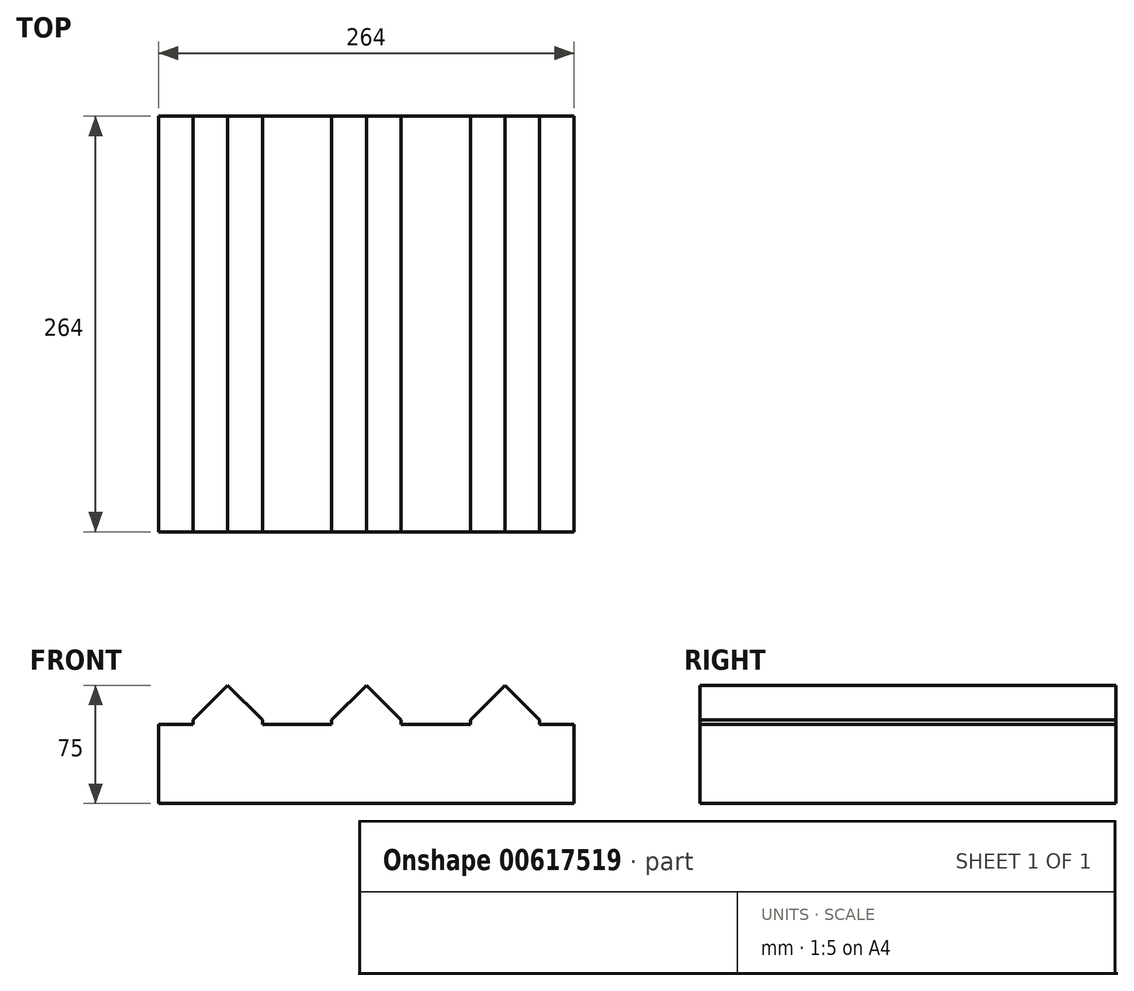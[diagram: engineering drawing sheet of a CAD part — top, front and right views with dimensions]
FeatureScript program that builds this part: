
annotation { "Feature Type Name" : "Feature", "Feature Type Description" : "" }
export const myFeature = defineFeature(function(context is Context, id is Id, definition is map)
    precondition{}
    {
        {
            var Q0;
            Q0=qCreatedBy(makeId("Top.planeOp"),FACE);
            var sketch = newSketch(context, id + "F0", { "sketchPlane" : qUnion([Q0])});
            skLineSegment(sketch, "E0.bottom", {"start": v(22, -22) * mm, "end": v(-22, -22) * mm});
            skLineSegment(sketch, "E0.top", {"start": v(22, 22) * mm, "end": v(-22, 22) * mm});
            skLineSegment(sketch, "E0.left", {"start": v(22, -22) * mm, "end": v(22, 22) * mm});
            skLineSegment(sketch, "E0.right", {"start": v(-22, -22) * mm, "end": v(-22, 22) * mm});
            skPoint(sketch, "E0.middle", {"position": v(0, 0) * mm});
            skLineSegment(sketch, "E1.bottom", {"start": v(-66, -22) * mm, "end": v(-110, -22) * mm});
            skLineSegment(sketch, "E1.top", {"start": v(-66, 22) * mm, "end": v(-110, 22) * mm});
            skLineSegment(sketch, "E1.left", {"start": v(-66, -22) * mm, "end": v(-66, 22) * mm});
            skLineSegment(sketch, "E1.right", {"start": v(-110, -22) * mm, "end": v(-110, 22) * mm});
            skPoint(sketch, "E1.middle", {"position": v(-88, 0) * mm});
            skPoint(sketch, "E1.middle.positionSnap0", {"position": v(-22, 0) * mm});
            skPoint(sketch, "E1.centerSnap0", {"position": v(-22, 0) * mm});
            skLineSegment(sketch, "E2.bottom", {"start": v(22, 66) * mm, "end": v(-22, 66) * mm});
            skLineSegment(sketch, "E2.top", {"start": v(22, 110) * mm, "end": v(-22, 110) * mm});
            skLineSegment(sketch, "E2.left", {"start": v(22, 66) * mm, "end": v(22, 110) * mm});
            skLineSegment(sketch, "E2.right", {"start": v(-22, 66) * mm, "end": v(-22, 110) * mm});
            skLineSegment(sketch, "E3.bottom", {"start": v(-66, 66) * mm, "end": v(-110, 66) * mm});
            skLineSegment(sketch, "E3.top", {"start": v(-66, 110) * mm, "end": v(-110, 110) * mm});
            skLineSegment(sketch, "E3.left", {"start": v(-66, 66) * mm, "end": v(-66, 110) * mm});
            skLineSegment(sketch, "E3.right", {"start": v(-110, 66) * mm, "end": v(-110, 110) * mm});
            skLineSegment(sketch, "E4.bottom", {"start": v(-132, 132) * mm, "end": v(132, 132) * mm});
            skLineSegment(sketch, "E4.top", {"start": v(-132, -132) * mm, "end": v(132, -132) * mm});
            skLineSegment(sketch, "E4.left", {"start": v(-132, 132) * mm, "end": v(-132, -132) * mm});
            skLineSegment(sketch, "E4.right", {"start": v(132, 132) * mm, "end": v(132, -132) * mm});
            skSolve(sketch);
        }
        {
            var Q0;
            Q0=makeQuery(id+"F0.imprint","IMPRINT",FACE,{"disambiguationData":[TD([[makeQuery(id+"F0.imprint","IMPRINT",EDGE,{"derivedFrom":sQuery(id+"F0.wireOp",EDGE,"E3.bottom")}),-1.0]])]});
            var Q1;
            Q1=makeQuery(id+"F0.imprint","IMPRINT",FACE,{"disambiguationData":[TD([[makeQuery(id+"F0.imprint","IMPRINT",EDGE,{"derivedFrom":sQuery(id+"F0.wireOp",EDGE,"E2.bottom")}),-1.0]])]});
            var Q2;
            Q2=makeQuery(id+"F0.imprint","IMPRINT",FACE,{"disambiguationData":[TD([[makeQuery(id+"F0.imprint","IMPRINT",EDGE,{"derivedFrom":sQuery(id+"F0.wireOp",EDGE,"E0.bottom")}),-1.0]])]});
            var Q3;
            Q3=makeQuery(id+"F0.imprint","IMPRINT",FACE,{"disambiguationData":[TD([[makeQuery(id+"F0.imprint","IMPRINT",EDGE,{"derivedFrom":sQuery(id+"F0.wireOp",EDGE,"E1.bottom")}),-1.0]])]});
            extrude(context, id + "F1", {"entities" : qUnion([Q0, Q1, Q2, Q3]), "depth" : 25 * mm, "offsetDistance" : 25 * mm});
        }
        {
            var Q0;
            Q0=makeQuery(id+"F1.opExtrude","SWEPT_BODY",BODY,{"disambiguationData":[OSD([sQuery(id+"F0.wireOp",EDGE,"E1.bottom"),sQuery(id+"F0.wireOp",EDGE,"E1.top"),sQuery(id+"F0.wireOp",EDGE,"E1.left"),sQuery(id+"F0.wireOp",EDGE,"E1.right")])]});
            var Q1;
            Q1=makeQuery(id+"F1.opExtrude","SWEPT_BODY",BODY,{"disambiguationData":[OSD([sQuery(id+"F0.wireOp",EDGE,"E3.bottom"),sQuery(id+"F0.wireOp",EDGE,"E3.top"),sQuery(id+"F0.wireOp",EDGE,"E3.left"),sQuery(id+"F0.wireOp",EDGE,"E3.right")])]});
            var Q2;
            Q2=qCreatedBy(makeId("Right.planeOp"),FACE);
            mirror(context, id + "F2", {"entities" : qUnion([Q0, Q1]), "mirrorPlane" : qUnion([Q2])});
        }
        {
            var Q0;
            Q0=makeQuery(id+"F1.opExtrude","SWEPT_BODY",BODY,{"disambiguationData":[OSD([sQuery(id+"F0.wireOp",EDGE,"E3.bottom"),sQuery(id+"F0.wireOp",EDGE,"E3.top"),sQuery(id+"F0.wireOp",EDGE,"E3.left"),sQuery(id+"F0.wireOp",EDGE,"E3.right")])]});
            var Q1;
            Q1=makeQuery(id+"F1.opExtrude","SWEPT_BODY",BODY,{"disambiguationData":[OSD([sQuery(id+"F0.wireOp",EDGE,"E2.bottom"),sQuery(id+"F0.wireOp",EDGE,"E2.top"),sQuery(id+"F0.wireOp",EDGE,"E2.left"),sQuery(id+"F0.wireOp",EDGE,"E2.right")])]});
            var Q2;
            Q2=makeQuery(id+"F2.opPattern","COPY",BODY,{"derivedFrom":makeQuery(id+"F1.opExtrude","SWEPT_BODY",BODY,{"disambiguationData":[OSD([sQuery(id+"F0.wireOp",EDGE,"E3.bottom"),sQuery(id+"F0.wireOp",EDGE,"E3.top"),sQuery(id+"F0.wireOp",EDGE,"E3.left"),sQuery(id+"F0.wireOp",EDGE,"E3.right")])]}),"instanceName":"1"});
            var Q3;
            Q3=qCreatedBy(makeId("Front.planeOp"),FACE);
            mirror(context, id + "F3", {"entities" : qUnion([Q0, Q1, Q2]), "mirrorPlane" : qUnion([Q3])});
        }
        {
            var Q0;
            Q0=makeQuery(id+"F0.imprint","IMPRINT",FACE,{"disambiguationData":[TD([[makeQuery(id+"F0.imprint","IMPRINT",EDGE,{"derivedFrom":sQuery(id+"F0.wireOp",EDGE,"E0.bottom")}),1.0]])]});
            var Q1;
            Q1=makeQuery(id+"F0.imprint","IMPRINT",FACE,{"disambiguationData":[TD([[makeQuery(id+"F0.imprint","IMPRINT",EDGE,{"derivedFrom":sQuery(id+"F0.wireOp",EDGE,"E1.bottom")}),-1.0]])]});
            var Q2;
            Q2=makeQuery(id+"F0.imprint","IMPRINT",FACE,{"disambiguationData":[TD([[makeQuery(id+"F0.imprint","IMPRINT",EDGE,{"derivedFrom":sQuery(id+"F0.wireOp",EDGE,"E0.bottom")}),-1.0]])]});
            var Q3;
            Q3=makeQuery(id+"F0.imprint","IMPRINT",FACE,{"disambiguationData":[TD([[makeQuery(id+"F0.imprint","IMPRINT",EDGE,{"derivedFrom":sQuery(id+"F0.wireOp",EDGE,"E3.bottom")}),-1.0]])]});
            var Q4;
            Q4=makeQuery(id+"F0.imprint","IMPRINT",FACE,{"disambiguationData":[TD([[makeQuery(id+"F0.imprint","IMPRINT",EDGE,{"derivedFrom":sQuery(id+"F0.wireOp",EDGE,"E2.bottom")}),-1.0]])]});
            extrude(context, id + "F4", {"entities" : qUnion([Q0, Q1, Q2, Q3, Q4]), "oppositeDirection" : true, "depth" : 50 * mm, "offsetDistance" : 25 * mm});
        }
        {
            var Q0;
            Q0=makeQuery(id+"F3.opPattern","COPY",FACE,{"derivedFrom":makeQuery(id+"F1.opExtrude","SWEPT_FACE",FACE,{"disambiguationData":[OSD([sQuery(id+"F0.wireOp",EDGE,"E3.bottom")])]}),"instanceName":"1"});
            var Q1;
            Q1=makeQuery(id+"F1.opExtrude","SWEPT_FACE",FACE,{"disambiguationData":[OSD([sQuery(id+"F0.wireOp",EDGE,"E1.top")])]});
            var Q2;
            Q2=makeQuery(id+"F1.opExtrude","SWEPT_FACE",FACE,{"disambiguationData":[OSD([sQuery(id+"F0.wireOp",EDGE,"E0.top")])]});
            var Q3;
            Q3=makeQuery(id+"F3.opPattern","COPY",FACE,{"derivedFrom":makeQuery(id+"F1.opExtrude","SWEPT_FACE",FACE,{"disambiguationData":[OSD([sQuery(id+"F0.wireOp",EDGE,"E2.bottom")])]}),"instanceName":"1"});
            var Q4;
            Q4=makeQuery(id+"F3.opPattern","COPY",FACE,{"derivedFrom":makeQuery(id+"F2.opPattern","COPY",FACE,{"derivedFrom":makeQuery(id+"F1.opExtrude","SWEPT_FACE",FACE,{"disambiguationData":[OSD([sQuery(id+"F0.wireOp",EDGE,"E3.bottom")])]}),"instanceName":"1"}),"instanceName":"1"});
            var Q5;
            Q5=makeQuery(id+"F2.opPattern","COPY",FACE,{"derivedFrom":makeQuery(id+"F1.opExtrude","SWEPT_FACE",FACE,{"disambiguationData":[OSD([sQuery(id+"F0.wireOp",EDGE,"E1.top")])]}),"instanceName":"1"});
            extrude(context, id + "F5", {"entities" : qUnion([Q0, Q1, Q2, Q3, Q4, Q5]), "operationType" : NewBodyOperationType.ADD, "depth" : 44 * mm, "offsetDistance" : 25 * mm});
        }
        {
            var Q0;
            Q0=makeQuery(id+"F3.opPattern","COPY",FACE,{"derivedFrom":makeQuery(id+"F1.opExtrude","SWEPT_FACE",FACE,{"disambiguationData":[OSD([sQuery(id+"F0.wireOp",EDGE,"E3.top")])]}),"instanceName":"1"});
            var Q1;
            Q1=makeQuery(id+"F3.opPattern","COPY",FACE,{"derivedFrom":makeQuery(id+"F1.opExtrude","SWEPT_FACE",FACE,{"disambiguationData":[OSD([sQuery(id+"F0.wireOp",EDGE,"E2.top")])]}),"instanceName":"1"});
            var Q2;
            Q2=makeQuery(id+"F3.opPattern","COPY",FACE,{"derivedFrom":makeQuery(id+"F2.opPattern","COPY",FACE,{"derivedFrom":makeQuery(id+"F1.opExtrude","SWEPT_FACE",FACE,{"disambiguationData":[OSD([sQuery(id+"F0.wireOp",EDGE,"E3.top")])]}),"instanceName":"1"}),"instanceName":"1"});
            var Q3;
            Q3=makeQuery(id+"F1.opExtrude","SWEPT_FACE",FACE,{"disambiguationData":[OSD([sQuery(id+"F0.wireOp",EDGE,"E3.top")])]});
            var Q4;
            Q4=makeQuery(id+"F1.opExtrude","SWEPT_FACE",FACE,{"disambiguationData":[OSD([sQuery(id+"F0.wireOp",EDGE,"E2.top")])]});
            var Q5;
            Q5=makeQuery(id+"F2.opPattern","COPY",FACE,{"derivedFrom":makeQuery(id+"F1.opExtrude","SWEPT_FACE",FACE,{"disambiguationData":[OSD([sQuery(id+"F0.wireOp",EDGE,"E3.top")])]}),"instanceName":"1"});
            extrude(context, id + "F6", {"entities" : qUnion([Q0, Q1, Q2, Q3, Q4, Q5]), "operationType" : NewBodyOperationType.ADD, "endBound" : BoundingType.SYMMETRIC, "depth" : 44 * mm, "offsetDistance" : 25 * mm});
        }
        {
            var Q0;
            {var subQ0=sQuery(id+"F0.wireOp",EDGE,"E3.right");var subQ1=sQuery(id+"F0.wireOp",EDGE,"E3.top");var subQ2=makeQuery(id+"F1.opExtrude","CAP_VERTEX",VERTEX,{"disambiguationData":[OSD([subQ1,subQ0])],"isStart":false});var subQ3=sQuery(id+"F0.wireOp",EDGE,"E3.bottom");var subQ4=sQuery(id+"F0.wireOp",EDGE,"E1.right");var subQ5=sQuery(id+"F0.wireOp",EDGE,"E1.top");var subQ6=makeQuery(id+"F1.opExtrude","CAP_EDGE",EDGE,{"disambiguationData":[OSD([subQ0])],"isStart":false});Q0=makeQuery(id+"F6.boolean.opBoolean","MERGE",EDGE,{"derivedFrom":[makeQuery(id+"F5.boolean.opBoolean","MERGE",EDGE,{"derivedFrom":[makeQuery(id+"F1.opExtrude","CAP_EDGE",EDGE,{"disambiguationData":[OSD([subQ4])],"isStart":false}),subQ6,makeQuery(id+"F3.opPattern","COPY",EDGE,{"derivedFrom":subQ6,"instanceName":"1"}),makeQuery(id+"F5.opExtrude","SWEPT_EDGE",EDGE,{"disambiguationData":[OSD([subQ5,subQ4]),TDD([makeQuery(id+"F1.opExtrude","CAP_VERTEX",VERTEX,{"disambiguationData":[OSD([subQ5,subQ4])],"isStart":false})])]}),makeQuery(id+"F5.opExtrude","SWEPT_EDGE",EDGE,{"disambiguationData":[OSD([subQ3,subQ0]),TDD([makeQuery(id+"F3.opPattern","COPY",VERTEX,{"derivedFrom":makeQuery(id+"F1.opExtrude","CAP_VERTEX",VERTEX,{"disambiguationData":[OSD([subQ3,subQ0])],"isStart":false}),"instanceName":"1"})])]})]}),makeQuery(id+"F6.opExtrude","SWEPT_EDGE",EDGE,{"disambiguationData":[OSD([subQ1,subQ0]),TDD([subQ2])]}),makeQuery(id+"F6.opExtrude","SWEPT_EDGE",EDGE,{"disambiguationData":[OSD([subQ1,subQ0]),TDD([makeQuery(id+"F3.opPattern","COPY",VERTEX,{"derivedFrom":subQ2,"instanceName":"1"})])]})]});}
            var Q1;
            {var subQ0=sQuery(id+"F0.wireOp",EDGE,"E3.left");var subQ1=sQuery(id+"F0.wireOp",EDGE,"E3.top");var subQ2=makeQuery(id+"F1.opExtrude","CAP_VERTEX",VERTEX,{"disambiguationData":[OSD([subQ1,subQ0])],"isStart":false});var subQ3=sQuery(id+"F0.wireOp",EDGE,"E3.bottom");var subQ4=sQuery(id+"F0.wireOp",EDGE,"E1.left");var subQ5=sQuery(id+"F0.wireOp",EDGE,"E1.top");var subQ6=makeQuery(id+"F1.opExtrude","CAP_EDGE",EDGE,{"disambiguationData":[OSD([subQ0])],"isStart":false});Q1=makeQuery(id+"F6.boolean.opBoolean","MERGE",EDGE,{"derivedFrom":[makeQuery(id+"F5.boolean.opBoolean","MERGE",EDGE,{"derivedFrom":[makeQuery(id+"F1.opExtrude","CAP_EDGE",EDGE,{"disambiguationData":[OSD([subQ4])],"isStart":false}),subQ6,makeQuery(id+"F3.opPattern","COPY",EDGE,{"derivedFrom":subQ6,"instanceName":"1"}),makeQuery(id+"F5.opExtrude","SWEPT_EDGE",EDGE,{"disambiguationData":[OSD([subQ5,subQ4]),TDD([makeQuery(id+"F1.opExtrude","CAP_VERTEX",VERTEX,{"disambiguationData":[OSD([subQ5,subQ4])],"isStart":false})])]}),makeQuery(id+"F5.opExtrude","SWEPT_EDGE",EDGE,{"disambiguationData":[OSD([subQ3,subQ0]),TDD([makeQuery(id+"F3.opPattern","COPY",VERTEX,{"derivedFrom":makeQuery(id+"F1.opExtrude","CAP_VERTEX",VERTEX,{"disambiguationData":[OSD([subQ3,subQ0])],"isStart":false}),"instanceName":"1"})])]})]}),makeQuery(id+"F6.opExtrude","SWEPT_EDGE",EDGE,{"disambiguationData":[OSD([subQ1,subQ0]),TDD([subQ2])]}),makeQuery(id+"F6.opExtrude","SWEPT_EDGE",EDGE,{"disambiguationData":[OSD([subQ1,subQ0]),TDD([makeQuery(id+"F3.opPattern","COPY",VERTEX,{"derivedFrom":subQ2,"instanceName":"1"})])]})]});}
            var Q2;
            {var subQ0=sQuery(id+"F0.wireOp",EDGE,"E2.right");var subQ1=sQuery(id+"F0.wireOp",EDGE,"E2.top");var subQ2=makeQuery(id+"F1.opExtrude","CAP_VERTEX",VERTEX,{"disambiguationData":[OSD([subQ1,subQ0])],"isStart":false});var subQ3=sQuery(id+"F0.wireOp",EDGE,"E2.bottom");var subQ4=sQuery(id+"F0.wireOp",EDGE,"E0.right");var subQ5=sQuery(id+"F0.wireOp",EDGE,"E0.top");var subQ6=makeQuery(id+"F1.opExtrude","CAP_EDGE",EDGE,{"disambiguationData":[OSD([subQ0])],"isStart":false});Q2=makeQuery(id+"F6.boolean.opBoolean","MERGE",EDGE,{"derivedFrom":[makeQuery(id+"F5.boolean.opBoolean","MERGE",EDGE,{"derivedFrom":[makeQuery(id+"F1.opExtrude","CAP_EDGE",EDGE,{"disambiguationData":[OSD([subQ4])],"isStart":false}),subQ6,makeQuery(id+"F3.opPattern","COPY",EDGE,{"derivedFrom":subQ6,"instanceName":"1"}),makeQuery(id+"F5.opExtrude","SWEPT_EDGE",EDGE,{"disambiguationData":[OSD([subQ5,subQ4]),TDD([makeQuery(id+"F1.opExtrude","CAP_VERTEX",VERTEX,{"disambiguationData":[OSD([subQ5,subQ4])],"isStart":false})])]}),makeQuery(id+"F5.opExtrude","SWEPT_EDGE",EDGE,{"disambiguationData":[OSD([subQ3,subQ0]),TDD([makeQuery(id+"F3.opPattern","COPY",VERTEX,{"derivedFrom":makeQuery(id+"F1.opExtrude","CAP_VERTEX",VERTEX,{"disambiguationData":[OSD([subQ3,subQ0])],"isStart":false}),"instanceName":"1"})])]})]}),makeQuery(id+"F6.opExtrude","SWEPT_EDGE",EDGE,{"disambiguationData":[OSD([subQ1,subQ0]),TDD([subQ2])]}),makeQuery(id+"F6.opExtrude","SWEPT_EDGE",EDGE,{"disambiguationData":[OSD([subQ1,subQ0]),TDD([makeQuery(id+"F3.opPattern","COPY",VERTEX,{"derivedFrom":subQ2,"instanceName":"1"})])]})]});}
            var Q3;
            {var subQ0=sQuery(id+"F0.wireOp",EDGE,"E2.left");var subQ1=sQuery(id+"F0.wireOp",EDGE,"E2.top");var subQ2=makeQuery(id+"F1.opExtrude","CAP_VERTEX",VERTEX,{"disambiguationData":[OSD([subQ1,subQ0])],"isStart":false});var subQ3=sQuery(id+"F0.wireOp",EDGE,"E2.bottom");var subQ4=sQuery(id+"F0.wireOp",EDGE,"E0.left");var subQ5=sQuery(id+"F0.wireOp",EDGE,"E0.top");var subQ6=makeQuery(id+"F1.opExtrude","CAP_EDGE",EDGE,{"disambiguationData":[OSD([subQ0])],"isStart":false});Q3=makeQuery(id+"F6.boolean.opBoolean","MERGE",EDGE,{"derivedFrom":[makeQuery(id+"F5.boolean.opBoolean","MERGE",EDGE,{"derivedFrom":[makeQuery(id+"F1.opExtrude","CAP_EDGE",EDGE,{"disambiguationData":[OSD([subQ4])],"isStart":false}),subQ6,makeQuery(id+"F3.opPattern","COPY",EDGE,{"derivedFrom":subQ6,"instanceName":"1"}),makeQuery(id+"F5.opExtrude","SWEPT_EDGE",EDGE,{"disambiguationData":[OSD([subQ5,subQ4]),TDD([makeQuery(id+"F1.opExtrude","CAP_VERTEX",VERTEX,{"disambiguationData":[OSD([subQ5,subQ4])],"isStart":false})])]}),makeQuery(id+"F5.opExtrude","SWEPT_EDGE",EDGE,{"disambiguationData":[OSD([subQ3,subQ0]),TDD([makeQuery(id+"F3.opPattern","COPY",VERTEX,{"derivedFrom":makeQuery(id+"F1.opExtrude","CAP_VERTEX",VERTEX,{"disambiguationData":[OSD([subQ3,subQ0])],"isStart":false}),"instanceName":"1"})])]})]}),makeQuery(id+"F6.opExtrude","SWEPT_EDGE",EDGE,{"disambiguationData":[OSD([subQ1,subQ0]),TDD([subQ2])]}),makeQuery(id+"F6.opExtrude","SWEPT_EDGE",EDGE,{"disambiguationData":[OSD([subQ1,subQ0]),TDD([makeQuery(id+"F3.opPattern","COPY",VERTEX,{"derivedFrom":subQ2,"instanceName":"1"})])]})]});}
            var Q4;
            {var subQ0=sQuery(id+"F0.wireOp",EDGE,"E3.left");var subQ1=sQuery(id+"F0.wireOp",EDGE,"E3.top");var subQ2=makeQuery(id+"F2.opPattern","COPY",VERTEX,{"derivedFrom":makeQuery(id+"F1.opExtrude","CAP_VERTEX",VERTEX,{"disambiguationData":[OSD([subQ1,subQ0])],"isStart":false}),"instanceName":"1"});var subQ3=sQuery(id+"F0.wireOp",EDGE,"E3.bottom");var subQ4=sQuery(id+"F0.wireOp",EDGE,"E1.left");var subQ5=sQuery(id+"F0.wireOp",EDGE,"E1.top");var subQ6=makeQuery(id+"F2.opPattern","COPY",EDGE,{"derivedFrom":makeQuery(id+"F1.opExtrude","CAP_EDGE",EDGE,{"disambiguationData":[OSD([subQ0])],"isStart":false}),"instanceName":"1"});Q4=makeQuery(id+"F6.boolean.opBoolean","MERGE",EDGE,{"derivedFrom":[makeQuery(id+"F5.boolean.opBoolean","MERGE",EDGE,{"derivedFrom":[makeQuery(id+"F2.opPattern","COPY",EDGE,{"derivedFrom":makeQuery(id+"F1.opExtrude","CAP_EDGE",EDGE,{"disambiguationData":[OSD([subQ4])],"isStart":false}),"instanceName":"1"}),subQ6,makeQuery(id+"F3.opPattern","COPY",EDGE,{"derivedFrom":subQ6,"instanceName":"1"}),makeQuery(id+"F5.opExtrude","SWEPT_EDGE",EDGE,{"disambiguationData":[OSD([subQ5,subQ4]),TDD([makeQuery(id+"F2.opPattern","COPY",VERTEX,{"derivedFrom":makeQuery(id+"F1.opExtrude","CAP_VERTEX",VERTEX,{"disambiguationData":[OSD([subQ5,subQ4])],"isStart":false}),"instanceName":"1"})])]}),makeQuery(id+"F5.opExtrude","SWEPT_EDGE",EDGE,{"disambiguationData":[OSD([subQ3,subQ0]),TDD([makeQuery(id+"F3.opPattern","COPY",VERTEX,{"derivedFrom":makeQuery(id+"F2.opPattern","COPY",VERTEX,{"derivedFrom":makeQuery(id+"F1.opExtrude","CAP_VERTEX",VERTEX,{"disambiguationData":[OSD([subQ3,subQ0])],"isStart":false}),"instanceName":"1"}),"instanceName":"1"})])]})]}),makeQuery(id+"F6.opExtrude","SWEPT_EDGE",EDGE,{"disambiguationData":[OSD([subQ1,subQ0]),TDD([subQ2])]}),makeQuery(id+"F6.opExtrude","SWEPT_EDGE",EDGE,{"disambiguationData":[OSD([subQ1,subQ0]),TDD([makeQuery(id+"F3.opPattern","COPY",VERTEX,{"derivedFrom":subQ2,"instanceName":"1"})])]})]});}
            var Q5;
            {var subQ0=sQuery(id+"F0.wireOp",EDGE,"E3.right");var subQ1=sQuery(id+"F0.wireOp",EDGE,"E3.top");var subQ2=makeQuery(id+"F2.opPattern","COPY",VERTEX,{"derivedFrom":makeQuery(id+"F1.opExtrude","CAP_VERTEX",VERTEX,{"disambiguationData":[OSD([subQ1,subQ0])],"isStart":false}),"instanceName":"1"});var subQ3=sQuery(id+"F0.wireOp",EDGE,"E3.bottom");var subQ4=sQuery(id+"F0.wireOp",EDGE,"E1.right");var subQ5=sQuery(id+"F0.wireOp",EDGE,"E1.top");var subQ6=makeQuery(id+"F2.opPattern","COPY",EDGE,{"derivedFrom":makeQuery(id+"F1.opExtrude","CAP_EDGE",EDGE,{"disambiguationData":[OSD([subQ0])],"isStart":false}),"instanceName":"1"});Q5=makeQuery(id+"F6.boolean.opBoolean","MERGE",EDGE,{"derivedFrom":[makeQuery(id+"F5.boolean.opBoolean","MERGE",EDGE,{"derivedFrom":[makeQuery(id+"F2.opPattern","COPY",EDGE,{"derivedFrom":makeQuery(id+"F1.opExtrude","CAP_EDGE",EDGE,{"disambiguationData":[OSD([subQ4])],"isStart":false}),"instanceName":"1"}),subQ6,makeQuery(id+"F3.opPattern","COPY",EDGE,{"derivedFrom":subQ6,"instanceName":"1"}),makeQuery(id+"F5.opExtrude","SWEPT_EDGE",EDGE,{"disambiguationData":[OSD([subQ5,subQ4]),TDD([makeQuery(id+"F2.opPattern","COPY",VERTEX,{"derivedFrom":makeQuery(id+"F1.opExtrude","CAP_VERTEX",VERTEX,{"disambiguationData":[OSD([subQ5,subQ4])],"isStart":false}),"instanceName":"1"})])]}),makeQuery(id+"F5.opExtrude","SWEPT_EDGE",EDGE,{"disambiguationData":[OSD([subQ3,subQ0]),TDD([makeQuery(id+"F3.opPattern","COPY",VERTEX,{"derivedFrom":makeQuery(id+"F2.opPattern","COPY",VERTEX,{"derivedFrom":makeQuery(id+"F1.opExtrude","CAP_VERTEX",VERTEX,{"disambiguationData":[OSD([subQ3,subQ0])],"isStart":false}),"instanceName":"1"}),"instanceName":"1"})])]})]}),makeQuery(id+"F6.opExtrude","SWEPT_EDGE",EDGE,{"disambiguationData":[OSD([subQ1,subQ0]),TDD([subQ2])]}),makeQuery(id+"F6.opExtrude","SWEPT_EDGE",EDGE,{"disambiguationData":[OSD([subQ1,subQ0]),TDD([makeQuery(id+"F3.opPattern","COPY",VERTEX,{"derivedFrom":subQ2,"instanceName":"1"})])]})]});}
            chamfer(context, id + "F7", {"entities" : qUnion([Q0, Q1, Q2, Q3, Q4, Q5]), "width" : 22 * mm, "tangentPropagation" : true});
        }
    });
